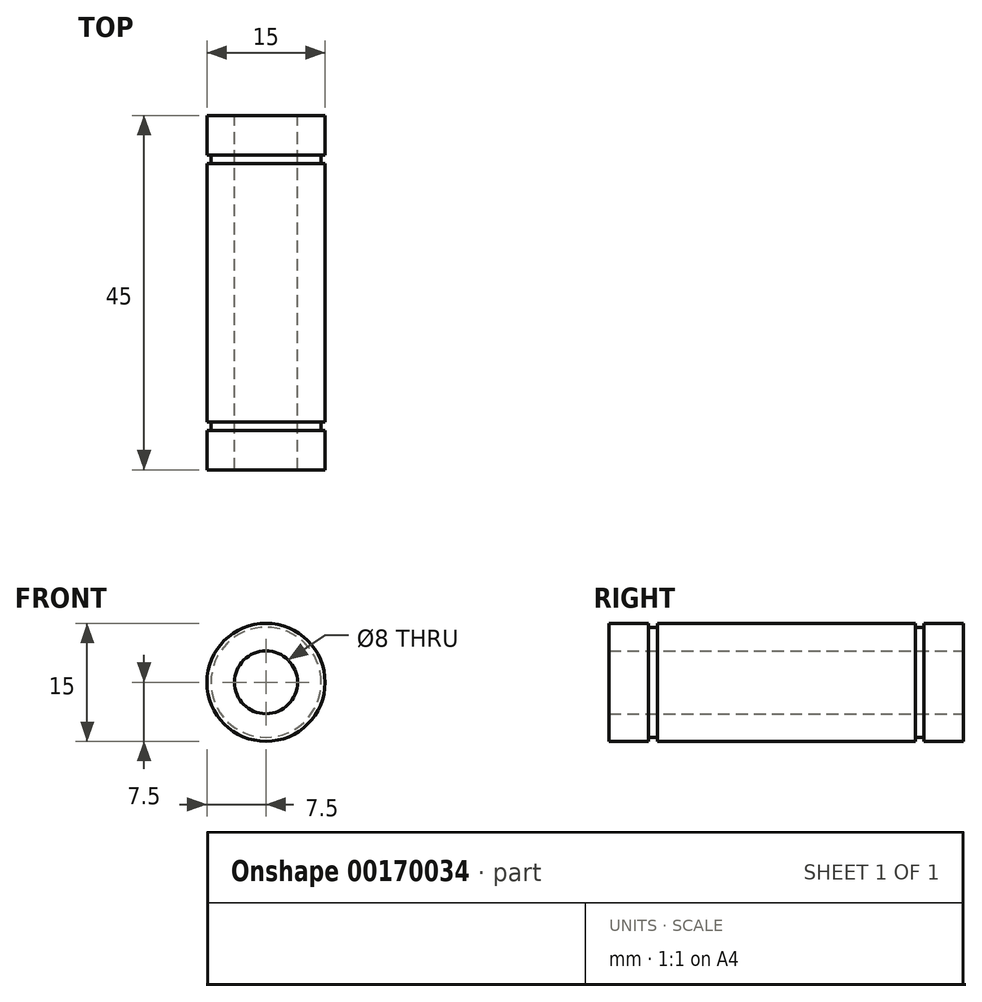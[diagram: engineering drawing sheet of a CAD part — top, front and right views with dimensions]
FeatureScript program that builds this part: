
annotation { "Feature Type Name" : "Feature", "Feature Type Description" : "" }
export const myFeature = defineFeature(function(context is Context, id is Id, definition is map)
    precondition{}
    {
        {
            var Q0;
            Q0=qCreatedBy(makeId("Front.planeOp"),FACE);
            var sketch = newSketch(context, id + "F0", { "sketchPlane" : qUnion([Q0])});
            skCircle(sketch, "E0", {"center": v(0, 0) * mm, "radius": 7.5 * mm});
            skCircle(sketch, "E1", {"center": v(0, 0) * mm, "radius": 4 * mm});
            skSolve(sketch);
        }
        {
            var Q0;
            Q0=qSketchRegion(id+"F0",true);
            extrude(context, id + "F1", {"entities" : qUnion([Q0]), "depth" : 5 * mm, "offsetDistance" : 25 * mm});
        }
        {
            var Q0;
            Q0=makeQuery(id+"F1.opExtrude","CAP_FACE",FACE,{"disambiguationData":[OSD([sQuery(id+"F0.wireOp",EDGE,"E0"),sQuery(id+"F0.wireOp",EDGE,"E1")])],"isStart":false});
            var sketch = newSketch(context, id + "F2", { "sketchPlane" : qUnion([Q0])});
            skCircle(sketch, "E2", {"center": v(0, 0) * mm, "radius": 7 * mm});
            skSolve(sketch);
        }
        {
            var Q0;
            Q0=makeQuery(id+"F2.imprint","IMPRINT",FACE,{"disambiguationData":[TD([[makeQuery(id+"F2.imprint","IMPRINT",EDGE,{"derivedFrom":sQuery(id+"F2.wireOp",EDGE,"E2")}),1.0]])]});
            var Q1;
            Q1=makeQuery(id+"F2.imprint","IMPRINT",FACE,{"disambiguationData":[TD([[makeQuery(id+"F2.imprint","IMPRINT",EDGE,{"derivedFrom":sQuery(id+"F2.wireOp",EDGE,"89afc66b-9a5b-46c4-a7c7-da3e920e76d60.MirrorC")}),-1.0]])]});
            extrude(context, id + "F3", {"entities" : qUnion([Q0, Q1]), "operationType" : NewBodyOperationType.ADD, "depth" : 1.1 * mm});
        }
        {
            var Q0;
            Q0=makeQuery(id+"F3.opExtrude","CAP_FACE",FACE,{"disambiguationData":[OSD([sQuery(id+"F0.wireOp",EDGE,"E1"),sQuery(id+"F2.wireOp",EDGE,"E2")])],"isStart":false});
            var sketch = newSketch(context, id + "F4", { "sketchPlane" : qUnion([Q0])});
            skCircle(sketch, "E3.0", {"center": v(0, 0) * mm, "radius": 7.5 * mm});
            skSolve(sketch);
        }
        {
            var Q0;
            Q0=makeQuery(id+"F4.imprint","IMPRINT",FACE,{"disambiguationData":[TD([[makeQuery(id+"F4.imprint","IMPRINT",EDGE,{"derivedFrom":makeQuery(id+"F3.opExtrude","CAP_EDGE",EDGE,{"disambiguationData":[OSD([sQuery(id+"F2.wireOp",EDGE,"E2")])],"isStart":false})}),1.0]])]});
            var Q1;
            Q1=makeQuery(id+"F4.imprint","IMPRINT",FACE,{"disambiguationData":[TD([[makeQuery(id+"F4.imprint","IMPRINT",EDGE,{"derivedFrom":sQuery(id+"F4.wireOp",EDGE,"E3.0")}),1.0]])]});
            extrude(context, id + "F5", {"entities" : qUnion([Q0, Q1]), "operationType" : NewBodyOperationType.ADD, "depth" : 32.8 * mm});
        }
        {
            var Q0;
            Q0=makeQuery(id+"F5.opExtrude","CAP_FACE",FACE,{"disambiguationData":[OSD([sQuery(id+"F0.wireOp",EDGE,"E1"),sQuery(id+"F4.wireOp",EDGE,"E3.0")])],"isStart":false});
            var sketch = newSketch(context, id + "F6", { "sketchPlane" : qUnion([Q0])});
            skCircle(sketch, "E4.0", {"center": v(0, 0) * mm, "radius": 7 * mm});
            skSolve(sketch);
        }
        {
            var Q0;
            Q0=makeQuery(id+"F6.imprint","IMPRINT",FACE,{"disambiguationData":[TD([[makeQuery(id+"F6.imprint","IMPRINT",EDGE,{"derivedFrom":sQuery(id+"F6.wireOp",EDGE,"E4.0")}),1.0]])]});
            extrude(context, id + "F7", {"entities" : qUnion([Q0]), "operationType" : NewBodyOperationType.ADD, "depth" : 1.1 * mm});
        }
        {
            var Q0;
            Q0=makeQuery(id+"F7.opExtrude","CAP_FACE",FACE,{"disambiguationData":[OSD([sQuery(id+"F0.wireOp",EDGE,"E1"),sQuery(id+"F6.wireOp",EDGE,"E4.0")])],"isStart":false});
            var sketch = newSketch(context, id + "F8", { "sketchPlane" : qUnion([Q0])});
            skCircle(sketch, "E5.0", {"center": v(0, 0) * mm, "radius": 7.5 * mm});
            skSolve(sketch);
        }
        {
            var Q0;
            Q0=makeQuery(id+"F8.imprint","IMPRINT",FACE,{"disambiguationData":[TD([[makeQuery(id+"F8.imprint","IMPRINT",EDGE,{"derivedFrom":sQuery(id+"F8.wireOp",EDGE,"E5.0")}),1.0]])]});
            var Q1;
            Q1=makeQuery(id+"F8.imprint","IMPRINT",FACE,{"disambiguationData":[TD([[makeQuery(id+"F8.imprint","IMPRINT",EDGE,{"derivedFrom":makeQuery(id+"F7.opExtrude","CAP_EDGE",EDGE,{"disambiguationData":[OSD([sQuery(id+"F6.wireOp",EDGE,"E4.0")])],"isStart":false})}),1.0]])]});
            extrude(context, id + "F9", {"entities" : qUnion([Q0, Q1]), "operationType" : NewBodyOperationType.ADD, "depth" : 5 * mm});
        }
    });
